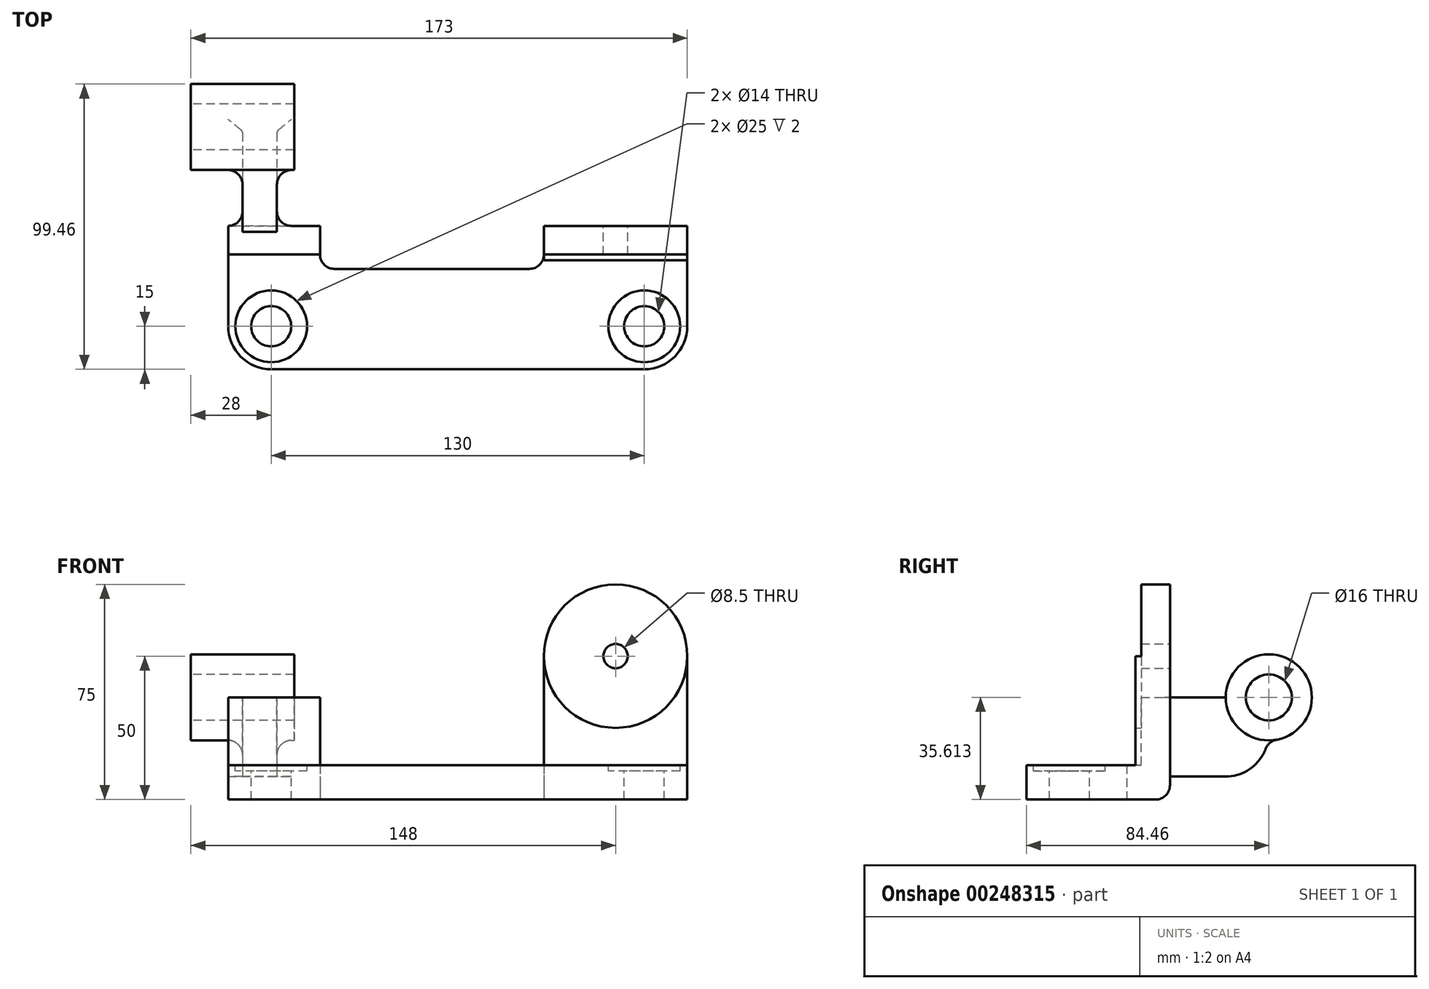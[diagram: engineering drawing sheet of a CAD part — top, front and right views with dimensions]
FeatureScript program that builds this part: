
annotation { "Feature Type Name" : "Feature", "Feature Type Description" : "" }
export const myFeature = defineFeature(function(context is Context, id is Id, definition is map)
    precondition{}
    {
        {
            var Q0;
            Q0=qCreatedBy(makeId("Top.planeOp"),FACE);
            var sketch = newSketch(context, id + "F0", { "sketchPlane" : qUnion([Q0])});
            skLineSegment(sketch, "E0.bottom", {"start": v(65, -25) * mm, "end": v(-65, -25) * mm});
            skLineSegment(sketch, "E0.top", {"start": v(80, 25) * mm, "end": v(30, 25) * mm});
            skLineSegment(sketch, "E0.left", {"start": v(80, -10) * mm, "end": v(80, 25) * mm});
            skLineSegment(sketch, "E0.right", {"start": v(-80, -10) * mm, "end": v(-80, 25) * mm});
            skPoint(sketch, "E0.middle", {"position": v(0, 0) * mm});
            skLineSegment(sketch, "E1.0", {"start": v(30, 10) * mm, "end": v(-48, 10) * mm});
            skLineSegment(sketch, "E2.0", {"start": v(-48, 10) * mm, "end": v(-48, 25) * mm});
            skLineSegment(sketch, "E3.0", {"start": v(30, 10) * mm, "end": v(30, 25) * mm});
            skLineSegment(sketch, "E4.trimOffspring", {"start": v(-48, 25) * mm, "end": v(-80, 25) * mm});
            skPoint(sketch, "E5.visualSharp", {"position": v(-80, -25) * mm});
            skArc(sketch, "E5.filletArc", {"start": v(-80, -10) * mm, "mid": v(-75.6, -20.6) * mm, "end": v(-65, -25) * mm});
            skPoint(sketch, "E6.visualSharp", {"position": v(80, -25) * mm});
            skArc(sketch, "E6.filletArc", {"start": v(65, -25) * mm, "mid": v(75.6, -20.6) * mm, "end": v(80, -10) * mm});
            skSolve(sketch);
        }
        {
            var Q0;
            Q0=makeQuery(id+"F0.imprint","IMPRINT",FACE,{"disambiguationData":[TD([[makeQuery(id+"F0.imprint","IMPRINT",EDGE,{"derivedFrom":sQuery(id+"F0.wireOp",EDGE,"E0.bottom")}),-1.0]])]});
            extrude(context, id + "F1", {"entities" : qUnion([Q0]), "depth" : 12 * mm});
        }
        {
            var Q0;
            Q0=makeQuery(id+"F1.opExtrude","SWEPT_EDGE",EDGE,{"disambiguationData":[OSD([sQuery(id+"F0.wireOp",EDGE,"E1.0"),sQuery(id+"F0.wireOp",EDGE,"E2.0")])]});
            var Q1;
            Q1=makeQuery(id+"F1.opExtrude","SWEPT_EDGE",EDGE,{"disambiguationData":[OSD([sQuery(id+"F0.wireOp",EDGE,"E1.0"),sQuery(id+"F0.wireOp",EDGE,"E3.0")])]});
            fillet(context, id + "F2", {"entities" : qUnion([Q0, Q1]), "radius" : 5 * mm, "tangentPropagation" : true, "allowEdgeOverflow" : false});
        }
        {
            var Q0;
            Q0=makeQuery(id+"F1.opExtrude","CAP_FACE",FACE,{"disambiguationData":[OSD([sQuery(id+"F0.wireOp",EDGE,"E0.bottom"),sQuery(id+"F0.wireOp",EDGE,"E0.top"),sQuery(id+"F0.wireOp",EDGE,"E0.left"),sQuery(id+"F0.wireOp",EDGE,"E0.right"),sQuery(id+"F0.wireOp",EDGE,"E1.0"),sQuery(id+"F0.wireOp",EDGE,"E2.0"),sQuery(id+"F0.wireOp",EDGE,"E3.0"),sQuery(id+"F0.wireOp",EDGE,"E4.trimOffspring"),sQuery(id+"F0.wireOp",EDGE,"E5.filletArc"),sQuery(id+"F0.wireOp",EDGE,"E6.filletArc")])],"isStart":false});
            var sketch = newSketch(context, id + "F3", { "sketchPlane" : qUnion([Q0])});
            skCircle(sketch, "E7", {"center": v(-65, -10) * mm, "radius": 7 * mm});
            skCircle(sketch, "E8", {"center": v(65, -10) * mm, "radius": 7 * mm});
            skSolve(sketch);
        }
        {
            var Q0;
            Q0=makeQuery(id+"F3.imprint","IMPRINT",FACE,{"disambiguationData":[TD([[makeQuery(id+"F3.imprint","IMPRINT",EDGE,{"derivedFrom":sQuery(id+"F3.wireOp",EDGE,"E8")}),1.0]])]});
            var Q1;
            Q1=makeQuery(id+"F3.imprint","IMPRINT",FACE,{"disambiguationData":[TD([[makeQuery(id+"F3.imprint","IMPRINT",EDGE,{"derivedFrom":sQuery(id+"F3.wireOp",EDGE,"E7")}),1.0]])]});
            extrude(context, id + "F4", {"entities" : qUnion([Q0, Q1]), "operationType" : NewBodyOperationType.REMOVE, "oppositeDirection" : true, "depth" : 25 * mm});
        }
        {
            var Q0;
            Q0=makeQuery(id+"F1.opExtrude","CAP_FACE",FACE,{"disambiguationData":[OSD([sQuery(id+"F0.wireOp",EDGE,"E0.bottom"),sQuery(id+"F0.wireOp",EDGE,"E0.top"),sQuery(id+"F0.wireOp",EDGE,"E0.left"),sQuery(id+"F0.wireOp",EDGE,"E0.right"),sQuery(id+"F0.wireOp",EDGE,"E1.0"),sQuery(id+"F0.wireOp",EDGE,"E2.0"),sQuery(id+"F0.wireOp",EDGE,"E3.0"),sQuery(id+"F0.wireOp",EDGE,"E4.trimOffspring"),sQuery(id+"F0.wireOp",EDGE,"E5.filletArc"),sQuery(id+"F0.wireOp",EDGE,"E6.filletArc")])],"isStart":false});
            var sketch = newSketch(context, id + "F5", { "sketchPlane" : qUnion([Q0])});
            skCircle(sketch, "E9", {"center": v(65, -10) * mm, "radius": 12.5 * mm});
            skCircle(sketch, "E10", {"center": v(-65, -10) * mm, "radius": 12.5 * mm});
            skSolve(sketch);
        }
        {
            var Q0;
            Q0=makeQuery(id+"F5.imprint","IMPRINT",FACE,{"disambiguationData":[TD([[makeQuery(id+"F5.imprint","IMPRINT",EDGE,{"derivedFrom":sQuery(id+"F5.wireOp",EDGE,"E9")}),1.0]])]});
            var Q1;
            Q1=makeQuery(id+"F5.imprint","IMPRINT",FACE,{"disambiguationData":[TD([[makeQuery(id+"F5.imprint","IMPRINT",EDGE,{"derivedFrom":sQuery(id+"F5.wireOp",EDGE,"E10")}),1.0]])]});
            extrude(context, id + "F6", {"entities" : qUnion([Q0, Q1]), "operationType" : NewBodyOperationType.REMOVE, "oppositeDirection" : true, "depth" : 2 * mm});
        }
        {
            var Q0;
            Q0=makeQuery(id+"F1.opExtrude","SWEPT_FACE",FACE,{"disambiguationData":[OSD([sQuery(id+"F0.wireOp",EDGE,"E0.top")])]});
            var sketch = newSketch(context, id + "F7", { "sketchPlane" : qUnion([Q0])});
            skLineSegment(sketch, "E11", {"start": v(-80, 0) * mm, "end": v(-80, 50) * mm});
            skLineSegment(sketch, "E12", {"start": v(-80, 50) * mm, "end": v(-30, 50) * mm, "construction": true});
            skLineSegment(sketch, "E13", {"start": v(-30, 50) * mm, "end": v(-30, 0) * mm});
            skLineSegment(sketch, "E14", {"start": v(-30, 0) * mm, "end": v(-80, 0) * mm});
            skLineSegment(sketch, "E15", {"start": v(-55, 73) * mm, "end": v(-55, -4.93) * mm, "construction": true});
            skPoint(sketch, "E15.startSnap0", {"position": v(-55, 50) * mm});
            skArc(sketch, "E16", {"start": v(-30, 50) * mm, "mid": v(-55, 75) * mm, "end": v(-80, 50) * mm});
            skSolve(sketch);
        }
        {
            var Q0;
            {var subQ2=sQuery(id+"F7.wireOp",EDGE,"E16");Q0=makeQuery(id+"F7.imprint","IMPRINT",FACE,{"disambiguationData":[TD([[makeQuery(id+"F7.imprint","IMPRINT",EDGE,{"derivedFrom":subQ2}),1.0]])]});}
            extrude(context, id + "F8", {"entities" : qUnion([Q0]), "operationType" : NewBodyOperationType.ADD, "oppositeDirection" : true, "depth" : 10 * mm});
        }
        {
            var Q0;
            Q0=makeQuery(id+"F8.opExtrude","CAP_FACE",FACE,{"disambiguationData":[OSD([sQuery(id+"F0.wireOp",EDGE,"E0.top"),sQuery(id+"F7.wireOp",EDGE,"E11"),sQuery(id+"F7.wireOp",EDGE,"E13"),sQuery(id+"F7.wireOp",EDGE,"E16")])],"isStart":false});
            var sketch = newSketch(context, id + "F9", { "sketchPlane" : qUnion([Q0])});
            skCircle(sketch, "E17", {"center": v(55, 50) * mm, "radius": 25 * mm});
            skSolve(sketch);
        }
        {
            var Q0;
            {var subQ0=sQuery(id+"F9.wireOp",EDGE,"E17");Q0=makeQuery(id+"F9.imprint","IMPRINT",FACE,{"disambiguationData":[TD([[makeQuery(id+"F9.imprint","IMPRINT",EDGE,{"disambiguationData":[OD(0.0)],"derivedFrom":subQ0}),-1.0]])]});}
            extrude(context, id + "F10", {"entities" : qUnion([Q0]), "operationType" : NewBodyOperationType.ADD, "depth" : 2 * mm});
        }
        {
            var Q0;
            Q0=makeQuery(id+"F8.opExtrude","CAP_EDGE",EDGE,{"disambiguationData":[OSD([sQuery(id+"F0.wireOp",EDGE,"E0.top")])],"isStart":false});
            var Q1;
            Q1=makeQuery(id+"F10.opExtrude","CAP_EDGE",EDGE,{"disambiguationData":[OSD([sQuery(id+"F9.wireOp",EDGE,"E17")])],"isStart":true});
            var Q2;
            Q2=makeQuery(id+"F1.opExtrude","CAP_EDGE",EDGE,{"disambiguationData":[OSD([sQuery(id+"F0.wireOp",EDGE,"E0.top")])],"isStart":true});
            fillet(context, id + "F11", {"entities" : qUnion([Q0, Q1, Q2]), "radius" : 5 * mm, "tangentPropagation" : true, "allowEdgeOverflow" : false});
        }
        {
            var Q0;
            Q0=makeQuery(id+"F1.opExtrude","SWEPT_FACE",FACE,{"disambiguationData":[OSD([sQuery(id+"F0.wireOp",EDGE,"E4.trimOffspring")])]});
            var sketch = newSketch(context, id + "F12", { "sketchPlane" : qUnion([Q0])});
            skLineSegment(sketch, "E18.bottom", {"start": v(48, 0) * mm, "end": v(80, 0) * mm});
            skLineSegment(sketch, "E18.top", {"start": v(48, 35.63) * mm, "end": v(80, 35.63) * mm});
            skLineSegment(sketch, "E18.left", {"start": v(48, 0) * mm, "end": v(48, 35.63) * mm});
            skLineSegment(sketch, "E18.right", {"start": v(80, 0) * mm, "end": v(80, 35.63) * mm});
            skSolve(sketch);
        }
        {
            var Q0;
            {var subQ0=sQuery(id+"F12.wireOp",EDGE,"E18.top");Q0=makeQuery(id+"F12.imprint","IMPRINT",FACE,{"disambiguationData":[TD([[makeQuery(id+"F12.imprint","IMPRINT",EDGE,{"derivedFrom":subQ0}),-1.0]])]});}
            extrude(context, id + "F13", {"entities" : qUnion([Q0]), "operationType" : NewBodyOperationType.ADD, "oppositeDirection" : true, "depth" : 10 * mm});
        }
        {
            var Q0;
            Q0=makeQuery(id+"F13.boolean.opBoolean","MERGE",FACE,{"derivedFrom":[makeQuery(id+"F1.opExtrude","SWEPT_FACE",FACE,{"disambiguationData":[OSD([sQuery(id+"F0.wireOp",EDGE,"E0.right")])]}),makeQuery(id+"F13.opExtrude","SWEPT_FACE",FACE,{"disambiguationData":[OSD([sQuery(id+"F12.wireOp",EDGE,"E18.right")])]})]});
            cPlane(context, id + "F14", {"entities" : qUnion([Q0]), "cplaneType" : CPlaneType.OFFSET, "offset" : 5 * mm, "oppositeDirection" : true, "width" : 150 * mm, "height" : 150 * mm});
        }
        {
            var Q0;
            Q0=qCreatedBy(id+"F14.planeOp",FACE);
            var sketch = newSketch(context, id + "F15", { "sketchPlane" : qUnion([Q0])});
            skLineSegment(sketch, "E19", {"start": v(-59.35, 35.65) * mm, "end": v(-59.35, 23) * mm});
            skPoint(sketch, "E20.visualSharp", {"position": v(-59.35, 8) * mm});
            skArc(sketch, "E20.filletArc", {"start": v(-59.35, 23) * mm, "mid": v(-54.96, 12.4) * mm, "end": v(-44.35, 8) * mm});
            skLineSegment(sketch, "E21", {"start": v(-22.96, 35.65) * mm, "end": v(-22.96, 8) * mm});
            skLineSegment(sketch, "E22", {"start": v(-59.35, 35.65) * mm, "end": v(-22.96, 35.65) * mm});
            skLineSegment(sketch, "E23", {"start": v(-44.35, 8) * mm, "end": v(-22.96, 8) * mm});
            skSolve(sketch);
        }
        {
            var Q0;
            Q0=makeQuery(id+"F15.imprint","IMPRINT",FACE,{"disambiguationData":[TD([[makeQuery(id+"F15.imprint","IMPRINT",EDGE,{"derivedFrom":sQuery(id+"F15.wireOp",EDGE,"E19")}),1.0]])]});
            extrude(context, id + "F16", {"entities" : qUnion([Q0]), "operationType" : NewBodyOperationType.ADD, "oppositeDirection" : true, "depth" : 12 * mm});
        }
        {
            var Q0;
            Q0=makeQuery(id+"F1.opExtrude","CAP_EDGE",EDGE,{"disambiguationData":[OSD([sQuery(id+"F0.wireOp",EDGE,"E4.trimOffspring")])],"isStart":true});
            var Q1;
            Q1=makeQuery(id+"F13.opExtrude","CAP_EDGE",EDGE,{"disambiguationData":[OSD([sQuery(id+"F0.wireOp",EDGE,"E4.trimOffspring")])],"isStart":false});
            fillet(context, id + "F17", {"entities" : qUnion([Q0, Q1]), "radius" : 5 * mm, "tangentPropagation" : true, "allowEdgeOverflow" : false});
        }
        {
            var Q0;
            Q0=makeQuery(id+"F15.imprint","IMPRINT",FACE,{"disambiguationData":[TD([[makeQuery(id+"F15.imprint","IMPRINT",EDGE,{"derivedFrom":sQuery(id+"F15.wireOp",EDGE,"E19")}),1.0]])]});
            var sketch = newSketch(context, id + "F18", { "sketchPlane" : qUnion([Q0])});
            skCircle(sketch, "E24", {"center": v(-59.46, 35.61) * mm, "radius": 15 * mm});
            skSolve(sketch);
        }
        {
            var Q0;
            {var subQ5=makeQuery(id+"F15.imprint","IMPRINT",EDGE,{"derivedFrom":sQuery(id+"F15.wireOp",EDGE,"E19")});Q0=makeQuery(id+"F18.imprint","IMPRINT",FACE,{"disambiguationData":[TD([[makeQuery(id+"F18.imprint","IMPRINT",EDGE,{"derivedFrom":subQ5}),-1.0]])]});}
            var Q1;
            {var subQ5=makeQuery(id+"F15.imprint","IMPRINT",EDGE,{"derivedFrom":sQuery(id+"F15.wireOp",EDGE,"E19")});Q1=makeQuery(id+"F18.imprint","IMPRINT",FACE,{"disambiguationData":[TD([[makeQuery(id+"F18.imprint","IMPRINT",EDGE,{"derivedFrom":subQ5}),1.0]])]});}
            extrude(context, id + "F19", {"entities" : qUnion([Q0, Q1]), "operationType" : NewBodyOperationType.ADD, "depth" : 36 * mm, "symmetric" : true});
        }
        {
            var Q0;
            Q0=makeQuery(id+"F19.opExtrude","CAP_FACE",FACE,{"disambiguationData":[OSD([sQuery(id+"F18.wireOp",EDGE,"E24")])],"isStart":false});
            var sketch = newSketch(context, id + "F20", { "sketchPlane" : qUnion([Q0])});
            skCircle(sketch, "E25", {"center": v(-59.46, 35.61) * mm, "radius": 8 * mm});
            skSolve(sketch);
        }
        {
            var Q0;
            Q0=makeQuery(id+"F20.imprint","IMPRINT",FACE,{"disambiguationData":[TD([[makeQuery(id+"F20.imprint","IMPRINT",EDGE,{"derivedFrom":sQuery(id+"F20.wireOp",EDGE,"E25")}),1.0]])]});
            extrude(context, id + "F21", {"entities" : qUnion([Q0]), "operationType" : NewBodyOperationType.REMOVE, "oppositeDirection" : true, "depth" : 52 * mm});
        }
        {
            var Q0;
            Q0=makeQuery(id+"F19.boolean.opBoolean","INTERSECT",EDGE,{"derivedFrom":[makeQuery(id+"F16.opExtrude","CAP_FACE",FACE,{"disambiguationData":[OSD([sQuery(id+"F15.wireOp",EDGE,"E19"),sQuery(id+"F15.wireOp",EDGE,"rSTIv4rB-Otmt-MCWk-2dUa-1LzobzHzvrNt"),sQuery(id+"F15.wireOp",EDGE,"E20.filletArc"),sQuery(id+"F15.wireOp",EDGE,"1lWsNmdN-3cwz-YJn5-fzL9-ztXgPEli604m"),sQuery(id+"F15.wireOp",EDGE,"c7HET4PF-hGXR-5r1F-VVed-QGXUasWQsZT3")])],"isStart":true}),makeQuery(id+"F19.opExtrude","SWEPT_FACE",FACE,{"disambiguationData":[OSD([sQuery(id+"F18.wireOp",EDGE,"E24")])]})]});
            var Q1;
            Q1=makeQuery(id+"F19.boolean.opBoolean","INTERSECT",EDGE,{"derivedFrom":[makeQuery(id+"F16.opExtrude","SWEPT_FACE",FACE,{"disambiguationData":[OSD([sQuery(id+"F15.wireOp",EDGE,"1lWsNmdN-3cwz-YJn5-fzL9-ztXgPEli604m")])]}),makeQuery(id+"F19.opExtrude","SWEPT_FACE",FACE,{"disambiguationData":[OSD([sQuery(id+"F18.wireOp",EDGE,"E24")])]})]});
            var Q2;
            Q2=makeQuery(id+"F19.boolean.opBoolean","INTERSECT",EDGE,{"derivedFrom":[makeQuery(id+"F16.opExtrude","CAP_FACE",FACE,{"disambiguationData":[OSD([sQuery(id+"F15.wireOp",EDGE,"E19"),sQuery(id+"F15.wireOp",EDGE,"rSTIv4rB-Otmt-MCWk-2dUa-1LzobzHzvrNt"),sQuery(id+"F15.wireOp",EDGE,"E20.filletArc"),sQuery(id+"F15.wireOp",EDGE,"1lWsNmdN-3cwz-YJn5-fzL9-ztXgPEli604m"),sQuery(id+"F15.wireOp",EDGE,"c7HET4PF-hGXR-5r1F-VVed-QGXUasWQsZT3")])],"isStart":false}),makeQuery(id+"F19.opExtrude","SWEPT_FACE",FACE,{"disambiguationData":[OSD([sQuery(id+"F18.wireOp",EDGE,"E24")])]})]});
            var Q3;
            Q3=makeQuery(id+"F19.boolean.opBoolean","INTERSECT",EDGE,{"derivedFrom":[makeQuery(id+"F16.opExtrude","SWEPT_FACE",FACE,{"disambiguationData":[OSD([sQuery(id+"F15.wireOp",EDGE,"E20.filletArc")])]}),makeQuery(id+"F19.opExtrude","SWEPT_FACE",FACE,{"disambiguationData":[OSD([sQuery(id+"F18.wireOp",EDGE,"E24")])]})]});
            fillet(context, id + "F22", {"entities" : qUnion([Q0, Q1, Q2, Q3]), "radius" : 5 * mm, "tangentPropagation" : true, "allowEdgeOverflow" : false});
        }
        {
            var Q0;
            {var subQ0=sQuery(id+"F0.wireOp",EDGE,"E4.trimOffspring");Q0=makeQuery(id+"F16.boolean.opBoolean","INTERSECT",EDGE,{"derivedFrom":[makeQuery(id+"F13.boolean.opBoolean","MERGE",FACE,{"derivedFrom":[makeQuery(id+"F1.opExtrude","SWEPT_FACE",FACE,{"disambiguationData":[OSD([subQ0])]}),makeQuery(id+"F13.opExtrude","CAP_FACE",FACE,{"disambiguationData":[OSD([subQ0,sQuery(id+"F12.wireOp",EDGE,"E18.top"),sQuery(id+"F12.wireOp",EDGE,"E18.left"),sQuery(id+"F12.wireOp",EDGE,"E18.right")])],"isStart":true})]}),makeQuery(id+"F16.opExtrude","CAP_FACE",FACE,{"disambiguationData":[OSD([sQuery(id+"F15.wireOp",EDGE,"E19"),sQuery(id+"F15.wireOp",EDGE,"E20.filletArc"),sQuery(id+"F15.wireOp",EDGE,"E21"),sQuery(id+"F15.wireOp",EDGE,"E22"),sQuery(id+"F15.wireOp",EDGE,"E23")])],"isStart":false})]});}
            var Q1;
            {var subQ0=sQuery(id+"F0.wireOp",EDGE,"E4.trimOffspring");Q1=makeQuery(id+"F16.boolean.opBoolean","INTERSECT",EDGE,{"derivedFrom":[makeQuery(id+"F13.boolean.opBoolean","MERGE",FACE,{"derivedFrom":[makeQuery(id+"F1.opExtrude","SWEPT_FACE",FACE,{"disambiguationData":[OSD([subQ0])]}),makeQuery(id+"F13.opExtrude","CAP_FACE",FACE,{"disambiguationData":[OSD([subQ0,sQuery(id+"F12.wireOp",EDGE,"E18.top"),sQuery(id+"F12.wireOp",EDGE,"E18.left"),sQuery(id+"F12.wireOp",EDGE,"E18.right")])],"isStart":true})]}),makeQuery(id+"F16.opExtrude","CAP_FACE",FACE,{"disambiguationData":[OSD([sQuery(id+"F15.wireOp",EDGE,"E19"),sQuery(id+"F15.wireOp",EDGE,"E20.filletArc"),sQuery(id+"F15.wireOp",EDGE,"E21"),sQuery(id+"F15.wireOp",EDGE,"E22"),sQuery(id+"F15.wireOp",EDGE,"E23")])],"isStart":true})]});}
            fillet(context, id + "F23", {"entities" : qUnion([Q0, Q1]), "radius" : 5 * mm, "tangentPropagation" : true, "allowEdgeOverflow" : false});
        }
        {
            var Q0;
            Q0=sQuery(id+"F7.wireOp",VERTEX,"E15.startSnap0");
            var Q1;
            Q1=makeQuery(id+"F1.opExtrude","SWEPT_BODY",BODY,{"disambiguationData":[OSD([sQuery(id+"F0.wireOp",EDGE,"E0.bottom"),sQuery(id+"F0.wireOp",EDGE,"E0.top"),sQuery(id+"F0.wireOp",EDGE,"E0.left"),sQuery(id+"F0.wireOp",EDGE,"E0.right"),sQuery(id+"F0.wireOp",EDGE,"E1.0"),sQuery(id+"F0.wireOp",EDGE,"E2.0"),sQuery(id+"F0.wireOp",EDGE,"E3.0"),sQuery(id+"F0.wireOp",EDGE,"E4.trimOffspring"),sQuery(id+"F0.wireOp",EDGE,"E5.filletArc"),sQuery(id+"F0.wireOp",EDGE,"E6.filletArc")])]});
            hole(context, id + "F24", {"style" : HoleStyle.SIMPLE, "endStyle" : HoleEndStyle.THROUGH, "standardTappedOrClearance" : lookupTablePath({ "standard" : "ISO", "engagement" : "75%", "pitch" : "1.5 mm", "size" : "M10", "type" : "Tapped" }), "standardBlindInLast" : lookupTablePath({ "standard" : "ISO", "engagement" : "75%", "pitch" : "1.5 mm", "size" : "M10", "type" : "Tapped" }), "holeDiameter" : 8.5 * mm, "showTappedDepth" : true, "tappedDepth" : 12 * mm, "tapClearance" : 3, "locations" : qUnion([Q0]), "scope" : qUnion([Q1]), "majorDiameter" : 10 * mm});
        }
    });
